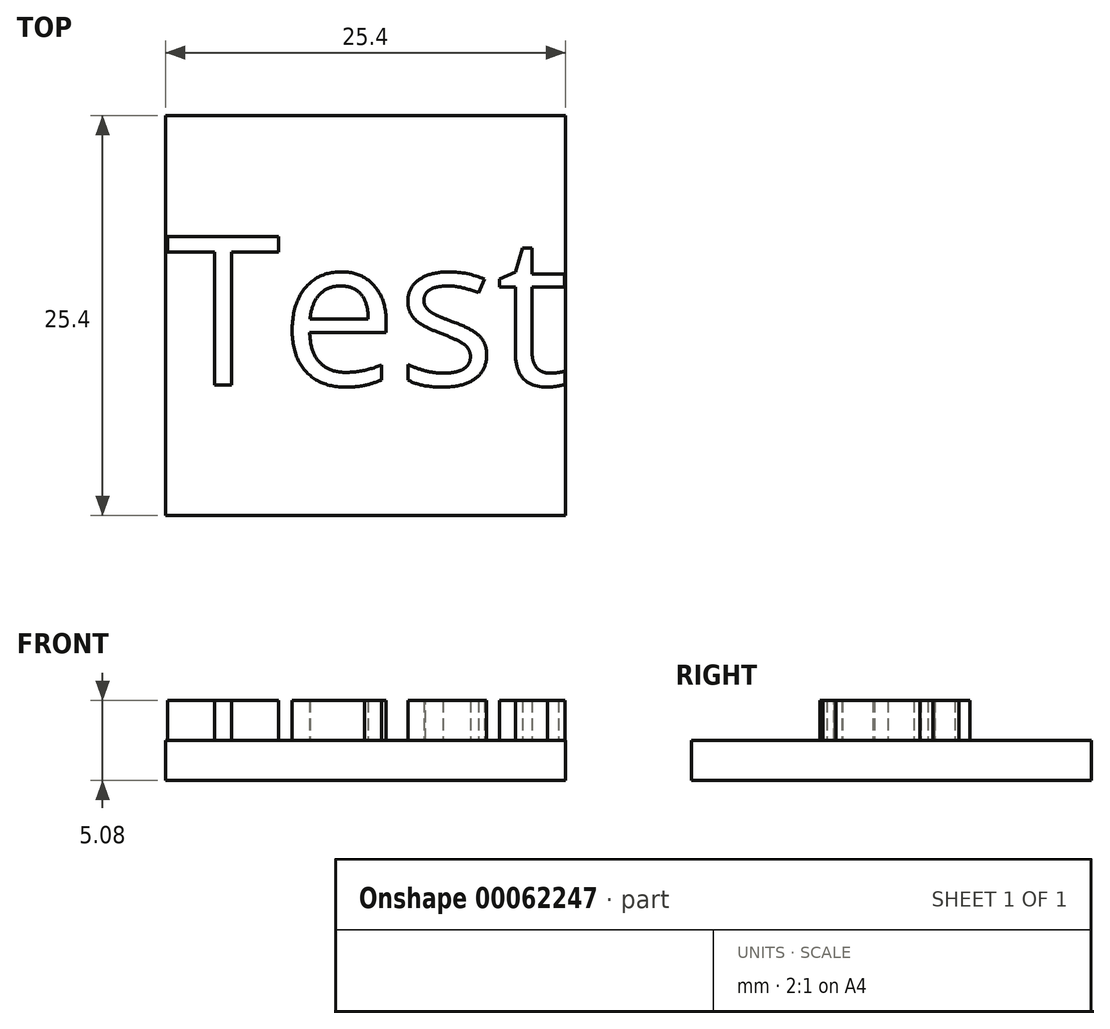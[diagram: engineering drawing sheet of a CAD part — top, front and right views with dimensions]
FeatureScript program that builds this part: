
annotation { "Feature Type Name" : "Feature", "Feature Type Description" : "" }
export const myFeature = defineFeature(function(context is Context, id is Id, definition is map)
    precondition{}
    {
        {
            var Q0;
            Q0=qCreatedBy(makeId("Top.planeOp"),FACE);
            var sketch = newSketch(context, id + "F1", { "sketchPlane" : qUnion([Q0])});
            skLineSegment(sketch, "E0.rect.bottom", {"start": v(-12.7, -12.7) * mm, "end": v(12.7, -12.7) * mm});
            skLineSegment(sketch, "E0.rect.top", {"start": v(-12.7, 12.7) * mm, "end": v(12.7, 12.7) * mm});
            skLineSegment(sketch, "E0.rect.left", {"start": v(-12.7, -12.7) * mm, "end": v(-12.7, 12.7) * mm});
            skLineSegment(sketch, "E0.rect.right", {"start": v(12.7, -12.7) * mm, "end": v(12.7, 12.7) * mm});
            skPoint(sketch, "E0.rect.middle", {"position": v(0, 0) * mm});
            skSolve(sketch);
        }
        {
            var Q0;
            Q0 = qSketchRegion(id + "F1", true);
            extrude(context, id + "F2", {"entities" : qUnion([Q0]), "depth" : 2.54 * mm});
        }
        {
            var Q0;
            Q0=makeQuery(id+"F2.opExtrude","CAP_FACE",FACE,{"disambiguationData":[OSD([sQuery(id+"F1.wireOp",EDGE,"E0.rect.bottom"),sQuery(id+"F1.wireOp",EDGE,"E0.rect.top"),sQuery(id+"F1.wireOp",EDGE,"E0.rect.left"),sQuery(id+"F1.wireOp",EDGE,"E0.rect.right")])],"isStart":false});
            var sketch = newSketch(context, id + "F0", { "sketchPlane" : qUnion([Q0])});
            skText(sketch, "E1", { "text": "Test", "fontName": "OpenSans-Regular.ttf"});
            const initialGuessF0  = {"E1": [-0.0127, -0.00442, 1, 0, 0.0095]};
            skSetInitialGuess(sketch, initialGuessF0);
            skSolve(sketch);
        }
        {
            var Q0;
            Q0 = qSketchRegion(id + "F0", true);
            extrude(context, id + "F3", {"entities" : qUnion([Q0]), "operationType" : NewBodyOperationType.ADD, "depth" : 2.54 * mm});
        }
    });
